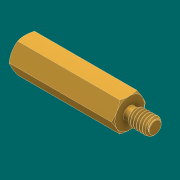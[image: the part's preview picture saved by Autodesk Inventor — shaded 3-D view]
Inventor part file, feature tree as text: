
AUTODESK INVENTOR PART (.ipt)
format: ipt  version: 2016 SP1 (Build 200210100, 210)  size: 531,968 bytes
history: native  units: mm
features: extrude x1
ambient origin geometry x8: Origin, YZ Plane, XZ Plane, XY Plane, X Axis, Y Axis, Z Axis, Center Point
bodies: Solid1 (feature_tree)
feature tree (1):
  extrude  "Extrude8"  [1 undecoded]
note: 1 required parameter value undecoded (feature->parameter linkage not recoverable at this tier; creation-order binding heuristic only, values carry confidence <= 0.55)
